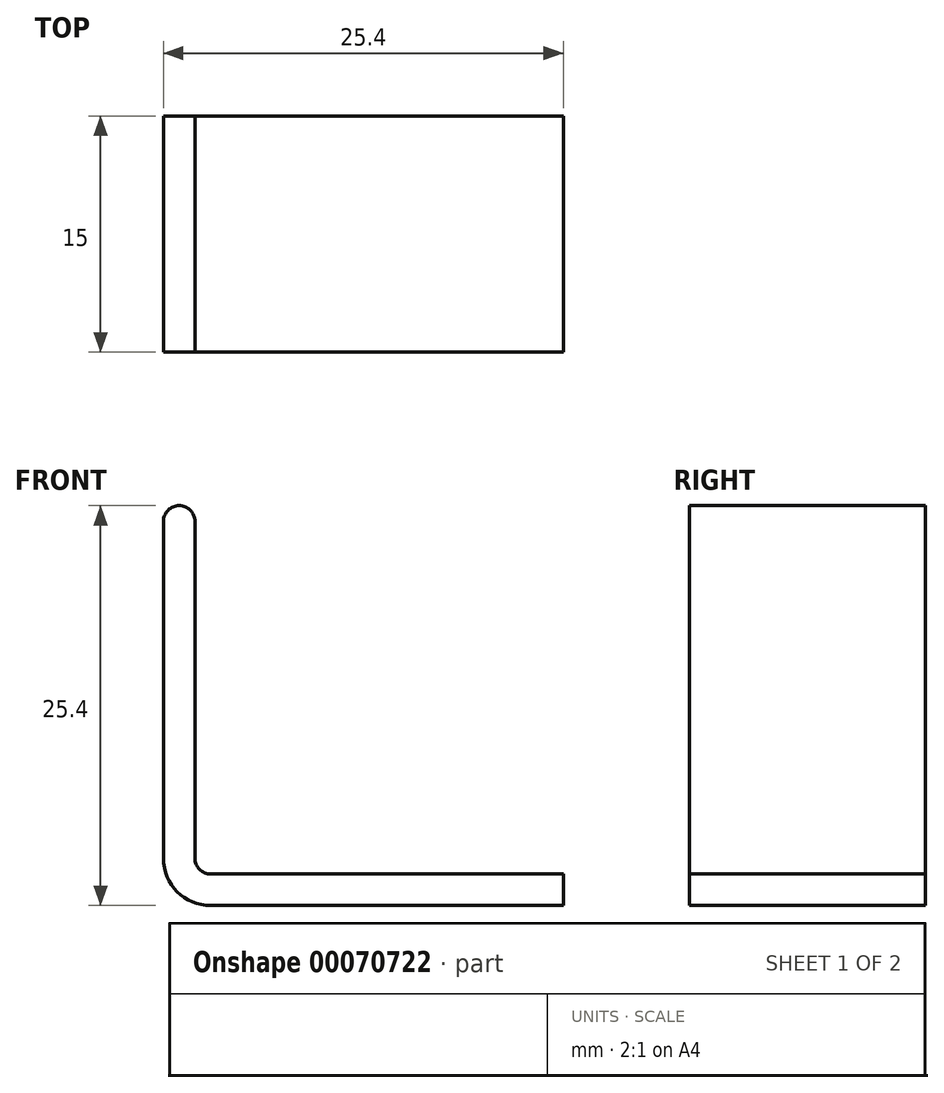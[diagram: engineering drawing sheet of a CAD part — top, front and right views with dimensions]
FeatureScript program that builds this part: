
annotation { "Feature Type Name" : "Feature", "Feature Type Description" : "" }
export const myFeature = defineFeature(function(context is Context, id is Id, definition is map)
    precondition{}
    {
        {
            var Q0;
            Q0=qCreatedBy(makeId("Front.planeOp"),FACE);
            var sketch = newSketch(context, id + "F0", { "sketchPlane" : qUnion([Q0])});
            skLineSegment(sketch, "E0", {"start": v(0, 3) * mm, "end": v(0, 25.4) * mm});
            skLineSegment(sketch, "E1", {"start": v(3, 0) * mm, "end": v(25.4, 0) * mm});
            skLineSegment(sketch, "E2", {"start": v(2, 25.4) * mm, "end": v(2, 3) * mm});
            skLineSegment(sketch, "E3", {"start": v(3, 2) * mm, "end": v(25.4, 2) * mm});
            skLineSegment(sketch, "E4", {"start": v(0, 25.4) * mm, "end": v(2, 25.4) * mm});
            skLineSegment(sketch, "E5", {"start": v(25.4, 2) * mm, "end": v(25.4, 0) * mm});
            skPoint(sketch, "E6.visualSharp", {"position": v(2, 2) * mm});
            skArc(sketch, "E6.filletArc", {"start": v(2, 3) * mm, "mid": v(2.3, 2.3) * mm, "end": v(3, 2) * mm});
            skPoint(sketch, "E7.visualSharp", {"position": v(0, 0) * mm});
            skArc(sketch, "E7.filletArc", {"start": v(0, 3) * mm, "mid": v(0.88, 0.88) * mm, "end": v(3, 0) * mm});
            skSolve(sketch);
        }
        {
            var Q0;
            Q0 = qSketchRegion(id + "F0", true);
            extrude(context, id + "F1", {"entities" : qUnion([Q0]), "depth" : 15 * mm, "symmetric" : true});
        }
        {
            var Q0;
            Q0=makeQuery(id+"F1.opExtrude","SWEPT_EDGE",EDGE,{"disambiguationData":[OSD([sQuery(id+"F0.wireOp",EDGE,"E2"),sQuery(id+"F0.wireOp",EDGE,"E4")])]});
            var Q1;
            Q1=makeQuery(id+"F1.opExtrude","SWEPT_EDGE",EDGE,{"disambiguationData":[OSD([sQuery(id+"F0.wireOp",EDGE,"E0"),sQuery(id+"F0.wireOp",EDGE,"E4")])]});
            fillet(context, id + "F2", {"entities" : qUnion([Q0, Q1]), "radius" : 1 * mm, "tangentPropagation" : true, "allowEdgeOverflow" : false});
        }
    });
